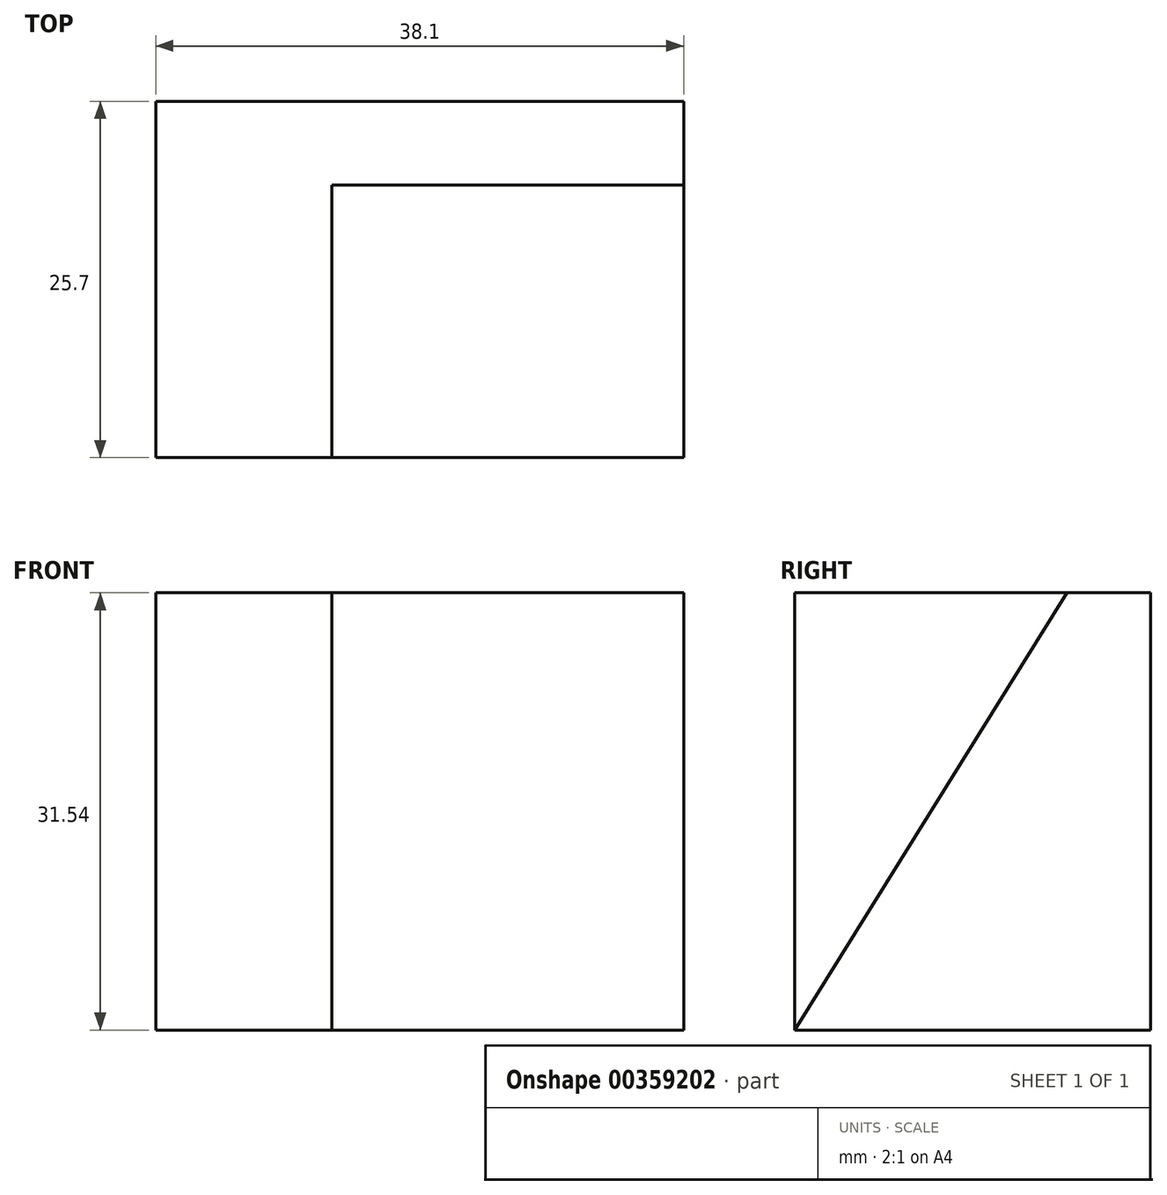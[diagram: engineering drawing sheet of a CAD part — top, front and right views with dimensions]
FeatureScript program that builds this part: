
annotation { "Feature Type Name" : "Feature", "Feature Type Description" : "" }
export const myFeature = defineFeature(function(context is Context, id is Id, definition is map)
    precondition{}
    {
        {
            var Q0;
            Q0=qCreatedBy(makeId("Right.planeOp"),FACE);
            var sketch = newSketch(context, id + "F0", { "sketchPlane" : qUnion([Q0])});
            skLineSegment(sketch, "E0", {"start": v(-12.07, 0) * mm, "end": v(-12.07, 31.54) * mm});
            skLineSegment(sketch, "E1", {"start": v(-12.07, 0) * mm, "end": v(-37.77, 0) * mm});
            skLineSegment(sketch, "E2", {"start": v(-37.77, 0) * mm, "end": v(-37.77, 31.54) * mm});
            skLineSegment(sketch, "E3", {"start": v(-37.77, 31.54) * mm, "end": v(-12.07, 31.54) * mm});
            skSolve(sketch);
        }
        {
            var Q0;
            Q0=makeQuery(id+"F0.imprint","IMPRINT",FACE,{"disambiguationData":[TD([[makeQuery(id+"F0.imprint","IMPRINT",EDGE,{"derivedFrom":sQuery(id+"F0.wireOp",EDGE,"E0")}),1.0]])]});
            extrude(context, id + "F1", {"entities" : qUnion([Q0]), "depth" : 38.1 * mm});
        }
        {
            var Q0;
            Q0=makeQuery(id+"F1.opExtrude","CAP_FACE",FACE,{"disambiguationData":[OSD([sQuery(id+"F0.wireOp",EDGE,"E0"),sQuery(id+"F0.wireOp",EDGE,"E1"),sQuery(id+"F0.wireOp",EDGE,"E2"),sQuery(id+"F0.wireOp",EDGE,"E3")])],"isStart":false});
            var sketch = newSketch(context, id + "F2", { "sketchPlane" : qUnion([Q0])});
            skLineSegment(sketch, "E4", {"start": v(-12.07, 31.54) * mm, "end": v(-18.1, 31.54) * mm});
            skLineSegment(sketch, "E5", {"start": v(-18.1, 31.54) * mm, "end": v(-37.77, 0) * mm});
            skSolve(sketch);
        }
        {
            var Q0;
            {var subQ0=sQuery(id+"F2.wireOp",EDGE,"E5");Q0=makeQuery(id+"F2.imprint","IMPRINT",FACE,{"disambiguationData":[TD([[makeQuery(id+"F2.imprint","IMPRINT",EDGE,{"derivedFrom":subQ0}),-1.0]])]});}
            extrude(context, id + "F3", {"entities" : qUnion([Q0]), "operationType" : NewBodyOperationType.ADD, "depth" : 25.4 * mm});
        }
        {
            var Q0;
            Q0=makeQuery(id+"F3.opExtrude","CAP_FACE",FACE,{"disambiguationData":[OSD([sQuery(id+"F0.wireOp",EDGE,"E2"),sQuery(id+"F0.wireOp",EDGE,"E3"),sQuery(id+"F2.wireOp",EDGE,"E5")])],"isStart":false});
            extrude(context, id + "F4", {"entities" : qUnion([Q0]), "operationType" : NewBodyOperationType.REMOVE, "oppositeDirection" : true, "depth" : 50.8 * mm});
        }
    });
